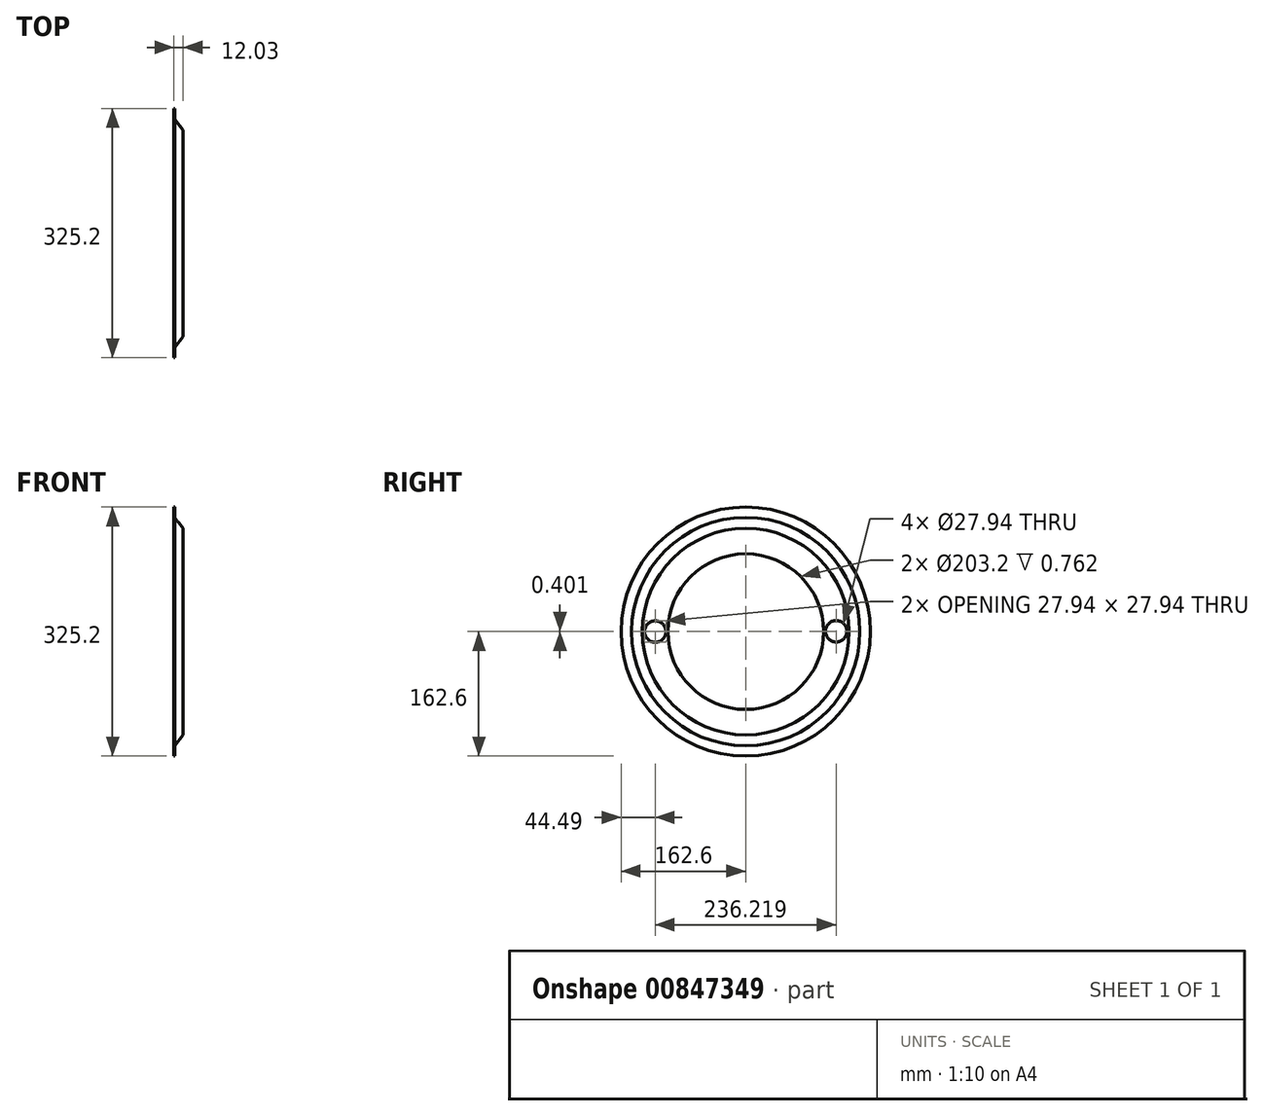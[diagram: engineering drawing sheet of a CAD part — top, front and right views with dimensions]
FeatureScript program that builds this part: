
annotation { "Feature Type Name" : "Feature", "Feature Type Description" : "" }
export const myFeature = defineFeature(function(context is Context, id is Id, definition is map)
    precondition{}
    {
        {
            var Q0;
            Q0=qCreatedBy(makeId("Top.planeOp"),FACE);
            var sketch = newSketch(context, id + "F0", { "sketchPlane" : qUnion([Q0])});
            skLineSegment(sketch, "E0", {"start": v(0, 0) * mm, "end": v(0.76, 0) * mm});
            skLineSegment(sketch, "E1.top", {"start": v(0, 162.6) * mm, "end": v(0.76, 162.6) * mm});
            skLineSegment(sketch, "E1.left", {"start": v(0, 148.97) * mm, "end": v(0, 162.6) * mm});
            skLineSegment(sketch, "E1.right", {"start": v(0.76, 148.02) * mm, "end": v(0.76, 162.6) * mm});
            skLineSegment(sketch, "E2", {"start": v(0.76, 148.97) * mm, "end": v(12.03, 134.89) * mm});
            skLineSegment(sketch, "E3", {"start": v(12.03, 134.89) * mm, "end": v(12.03, 101.6) * mm});
            skLineSegment(sketch, "E4", {"start": v(11.27, 101.6) * mm, "end": v(11.27, 134.89) * mm});
            skLineSegment(sketch, "E5", {"start": v(11.27, 134.89) * mm, "end": v(0.76, 148.02) * mm});
            skLineSegment(sketch, "E6", {"start": v(11.27, 101.6) * mm, "end": v(12.03, 101.6) * mm});
            skPoint(sketch, "E7.orphan", {"position": v(0, 101.6) * mm});
            skPoint(sketch, "E1.bottom.end.orphan", {"position": v(0.76, 21.89) * mm});
            skPoint(sketch, "E1.bottom.start.orphan", {"position": v(0, 21.89) * mm});
            skPoint(sketch, "E8.start.orphan", {"position": v(12.03, 21.89) * mm});
            skLineSegment(sketch, "E9", {"start": v(0.76, 148.97) * mm, "end": v(0, 149.92) * mm});
            skLineSegment(sketch, "E10", {"start": v(0.76, 148.02) * mm, "end": v(0, 148.97) * mm});
            skPoint(sketch, "E11.orphan", {"position": v(0.76, 101.6) * mm});
            skLineSegment(sketch, "E12.MirrorCS", {"start": v(11.27, -101.6) * mm, "end": v(12.03, -101.6) * mm});
            skLineSegment(sketch, "E13.MirrorCS", {"start": v(0.76, -148.97) * mm, "end": v(0, -149.92) * mm});
            skLineSegment(sketch, "E14.MirrorCS", {"start": v(0.76, -148.02) * mm, "end": v(0, -148.97) * mm});
            skLineSegment(sketch, "E15.MirrorCS", {"start": v(0, -162.6) * mm, "end": v(0.76, -162.6) * mm});
            skLineSegment(sketch, "E16.MirrorCS", {"start": v(11.27, -101.6) * mm, "end": v(11.27, -134.89) * mm});
            skLineSegment(sketch, "E17.MirrorCS", {"start": v(12.03, -134.89) * mm, "end": v(12.03, -101.6) * mm});
            skPoint(sketch, "E18.MirrorP", {"position": v(0.76, -101.6) * mm});
            skLineSegment(sketch, "E19.MirrorCS", {"start": v(0, -148.97) * mm, "end": v(0, -162.6) * mm});
            skLineSegment(sketch, "E20.MirrorCS", {"start": v(0.76, -148.97) * mm, "end": v(12.03, -134.89) * mm});
            skLineSegment(sketch, "E21.MirrorCS", {"start": v(11.27, -134.89) * mm, "end": v(0.76, -148.02) * mm});
            skLineSegment(sketch, "E22.MirrorCS", {"start": v(0.76, -148.02) * mm, "end": v(0.76, -162.6) * mm});
            skPoint(sketch, "E23.MirrorP", {"position": v(0, -101.6) * mm});
            skSolve(sketch);
        }
        {
            var Q0;
            Q0 = qSketchRegion(id + "F0", true);
            var Q1;
            Q1=sQuery(id+"F0.wireOp",EDGE,"E0");
            revolve(context, id + "F1", {"surfaceOperationType" : NewSurfaceOperationType.NEW, "entities" : qUnion([Q0]), "axis" : qUnion([Q1]), "revolveType" : RevolveType.FULL});
        }
        {
            var Q0;
            Q0=makeQuery(id+"F1.opRevolve","SWEPT_FACE",FACE,{"disambiguationData":[OSD([sQuery(id+"F0.wireOp",EDGE,"E3")])]});
            var sketch = newSketch(context, id + "F2", { "sketchPlane" : qUnion([Q0])});
            skCircle(sketch, "E24", {"center": v(-118.11, 0) * mm, "radius": 13.97 * mm});
            skCircle(sketch, "E25", {"center": v(118.1, 0.4) * mm, "radius": 13.97 * mm});
            skPoint(sketch, "E26.orphan", {"position": v(0, 0) * mm});
            skSolve(sketch);
        }
        {
            var Q0;
            Q0=sQuery(id+"F2.wireOp",VERTEX,"E24.center");
            var Q1;
            Q1=sQuery(id+"F2.wireOp",VERTEX,"E25.center");
            var Q2;
            Q2=makeQuery(id+"F1.opRevolve","SWEPT_BODY",BODY,{"disambiguationData":[OSD([sQuery(id+"F0.wireOp",EDGE,"E1.top"),sQuery(id+"F0.wireOp",EDGE,"E1.left"),sQuery(id+"F0.wireOp",EDGE,"E1.right"),sQuery(id+"F0.wireOp",EDGE,"E2"),sQuery(id+"F0.wireOp",EDGE,"E3"),sQuery(id+"F0.wireOp",EDGE,"E4"),sQuery(id+"F0.wireOp",EDGE,"E5"),sQuery(id+"F0.wireOp",EDGE,"E6"),sQuery(id+"F0.wireOp",EDGE,"E10")])]});
            var Q3;
            Q3=makeQuery(id+"F1.opRevolve","SWEPT_BODY",BODY,{"disambiguationData":[OSD([sQuery(id+"F0.wireOp",EDGE,"E15.MirrorCS"),sQuery(id+"F0.wireOp",EDGE,"E14.MirrorCS"),sQuery(id+"F0.wireOp",EDGE,"E19.MirrorCS"),sQuery(id+"F0.wireOp",EDGE,"E22.MirrorCS"),sQuery(id+"F0.wireOp",EDGE,"E12.MirrorCS"),sQuery(id+"F0.wireOp",EDGE,"E17.MirrorCS"),sQuery(id+"F0.wireOp",EDGE,"E20.MirrorCS"),sQuery(id+"F0.wireOp",EDGE,"E21.MirrorCS"),sQuery(id+"F0.wireOp",EDGE,"E16.MirrorCS")])]});
            hole(context, id + "F3", {"style" : HoleStyle.SIMPLE, "endStyle" : HoleEndStyle.THROUGH, "holeDiameter" : 27.94 * mm, "majorDiameter" : 6.35 * mm, "isTappedThrough" : true, "tappedDepth" : 12.7 * mm, "tapClearance" : 3, "locations" : qUnion([Q0, Q1]), "scope" : qUnion([Q2, Q3])});
        }
    });
